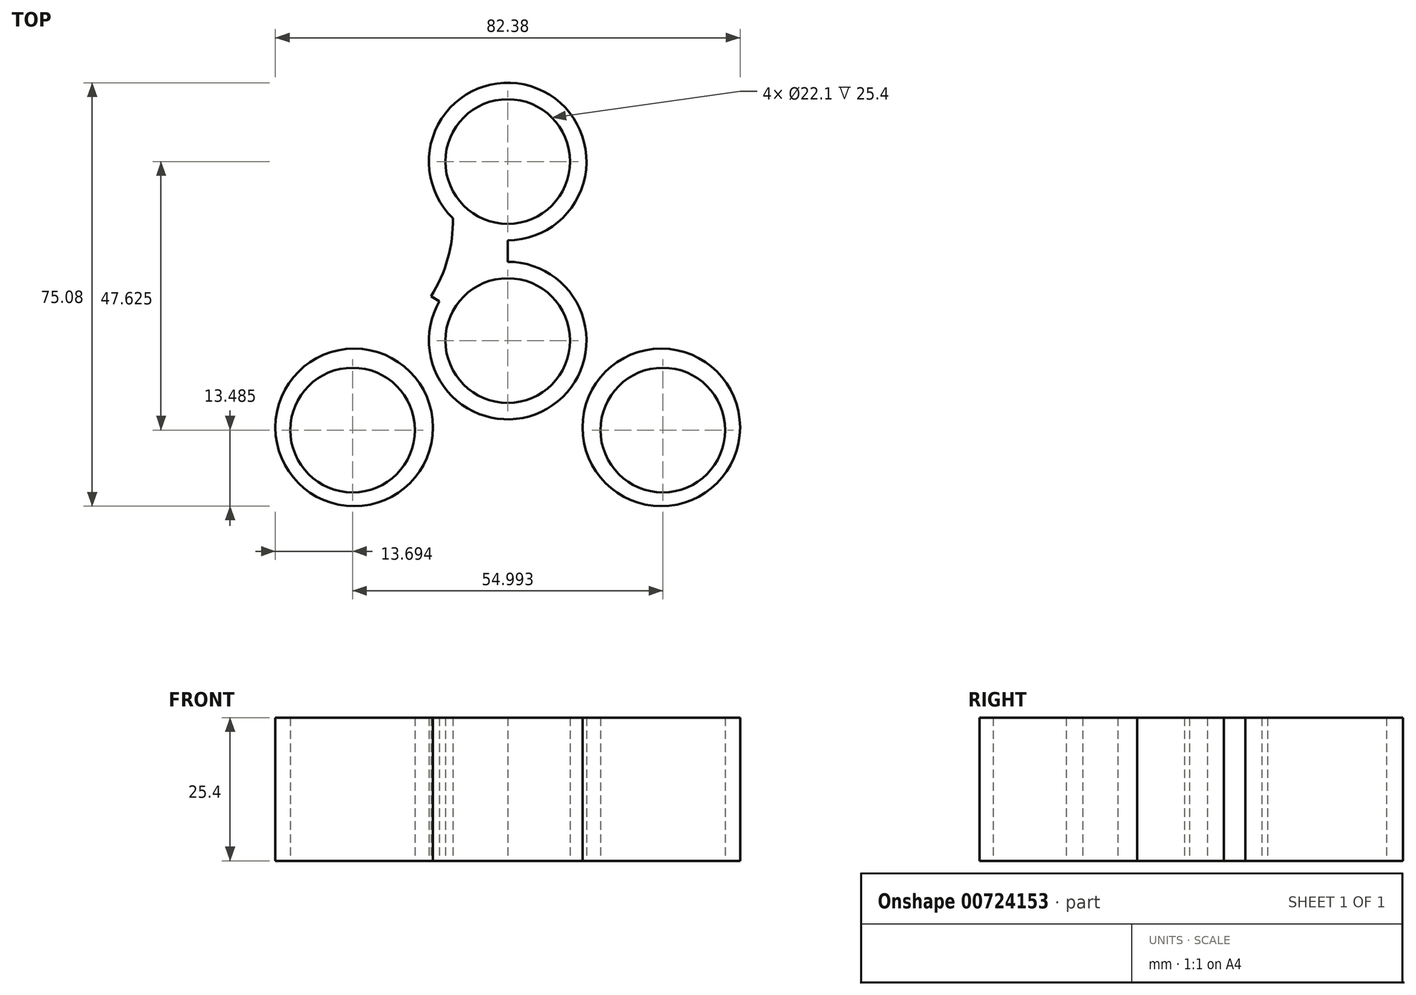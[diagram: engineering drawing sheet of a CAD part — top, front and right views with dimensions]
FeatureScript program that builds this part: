
annotation { "Feature Type Name" : "Feature", "Feature Type Description" : "" }
export const myFeature = defineFeature(function(context is Context, id is Id, definition is map)
    precondition{}
    {
        {
            var Q0;
            Q0=qCreatedBy(makeId("Top.planeOp"),FACE);
            var sketch = newSketch(context, id + "F0", { "sketchPlane" : qUnion([Q0])});
            skCircle(sketch, "E0", {"center": v(0, 0) * mm, "radius": 11.05 * mm});
            skCircle(sketch, "E1", {"center": v(0, 0) * mm, "radius": 13.97 * mm});
            skLineSegment(sketch, "E2", {"start": v(0, 0) * mm, "end": v(0, 31.75) * mm});
            skCircle(sketch, "E3", {"center": v(0, 31.75) * mm, "radius": 11.05 * mm});
            skCircle(sketch, "E4", {"center": v(0, 31.75) * mm, "radius": 13.97 * mm});
            skCircle(sketch, "E5.1.0", {"center": v(-27.22, -15.4) * mm, "radius": 13.97 * mm});
            skCircle(sketch, "E5.2.0", {"center": v(27.22, -15.4) * mm, "radius": 13.97 * mm});
            skPoint(sketch, "E5.center", {"position": v(0, 0.32) * mm});
            skCircle(sketch, "E6.1.0", {"center": v(-27.5, -15.87) * mm, "radius": 11.05 * mm});
            skCircle(sketch, "E6.2.0", {"center": v(27.5, -15.87) * mm, "radius": 11.05 * mm});
            skLineSegment(sketch, "E7", {"start": v(0, 0) * mm, "end": v(-26.4, 15.24) * mm});
            skArc(sketch, "E8", {"start": v(-24.63, -1.66) * mm, "mid": v(-13.65, 7.77) * mm, "end": v(-9.71, 21.7) * mm});
            skArc(sketch, "E9.1.0", {"start": v(13.76, -20.5) * mm, "mid": v(0.1, -15.7) * mm, "end": v(-13.94, -19.26) * mm});
            skArc(sketch, "E9.2.0", {"start": v(10.87, 22.16) * mm, "mid": v(13.55, 7.93) * mm, "end": v(23.65, -2.44) * mm});
            skSolve(sketch);
        }
        {
            var Q0;
            Q0 = qSketchRegion(id + "F0", true);
            extrude(context, id + "F1", {"entities" : qUnion([Q0]), "depth" : 25.4 * mm, "offsetDistance" : 25.4 * mm});
        }
    });
